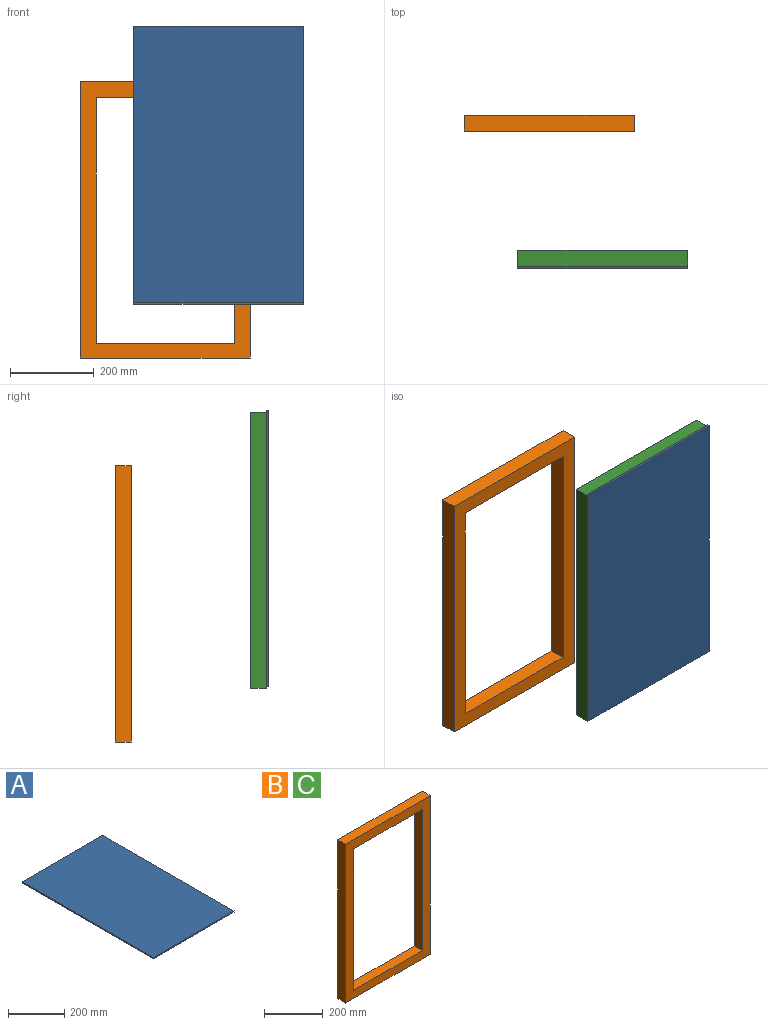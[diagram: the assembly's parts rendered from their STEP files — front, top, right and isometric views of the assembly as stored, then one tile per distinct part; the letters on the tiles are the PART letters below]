
ASSEMBLY  parts=3 mates=1
PART A: 6 faces, bbox 406.4x660.4x5.1 mm
  f0: plane 660.4x5.08mm, normal (1,0,0), area 3354.8mm2, adj f1,f3,f4,f5
  f1: plane 406.4x5.08mm, normal (0,1,0), area 2064.5mm2, adj f0,f2,f4,f5
  f2: plane 660.4x5.08mm, normal (-1,0,0), area 3354.8mm2, adj f1,f3,f4,f5
  f3: plane 406.4x5.08mm, normal (0,-1,0), area 2064.5mm2, adj f0,f2,f4,f5
  f4: plane 660.4x406.4mm, normal (0,0,1), area 268386.6mm2, adj f0,f1,f2,f3
  f5: plane 660.4x406.4mm, normal (0,0,-1), area 268386.6mm2, adj f0,f1,f2,f3
PART B: 10 faces, bbox 406.4x38.1x660.4 mm
  f0: plane 587.98x38.1mm, normal (1,0,0), area 22402.2mm2, adj f1,f3,f6,f7
  f1: plane 660.4x406.4mm, normal (0,1,0), area 74234.6mm2, adj f0,f2,f4,f5,f6,f7,f8,f9
  f2: plane 660.4x38.1mm, normal (-1,0,0), area 25161.2mm2, adj f1,f3,f4,f5
  f3: plane 660.4x406.4mm, normal (0,-1,0), area 74234.6mm2, adj f0,f2,f4,f5,f6,f7,f8,f9
  f4: plane 406.4x38.1mm, normal (0,0,1), area 15483.8mm2, adj f1,f2,f3,f9
  f5: plane 406.4x38.1mm, normal (0,0,-1), area 15483.8mm2, adj f1,f2,f3,f9
  f6: plane 330.2x38.1mm, normal (0,0,-1), area 12580.6mm2, adj f0,f1,f3,f8
  f7: plane 330.2x38.1mm, normal (0,0,1), area 12580.6mm2, adj f0,f1,f3,f8
  f8: plane 587.98x38.1mm, normal (-1,0,0), area 22402.2mm2, adj f1,f3,f6,f7
  f9: plane 660.4x38.1mm, normal (1,0,0), area 25161.2mm2, adj f1,f3,f4,f5
PART C: same geometry as B
PLACE A rot(axis=(-1,0,0),90deg) t=(1126.9,-332.76,233.18)mm
PLACE B t=(815.03,14.58,-230.37)mm
PLACE C t=(942.75,-308.63,-101.97)mm
MATE fastened A.f4 <-> C.f3  axis (0,1,0) through (1126.9,-327.68,233.18)mm
